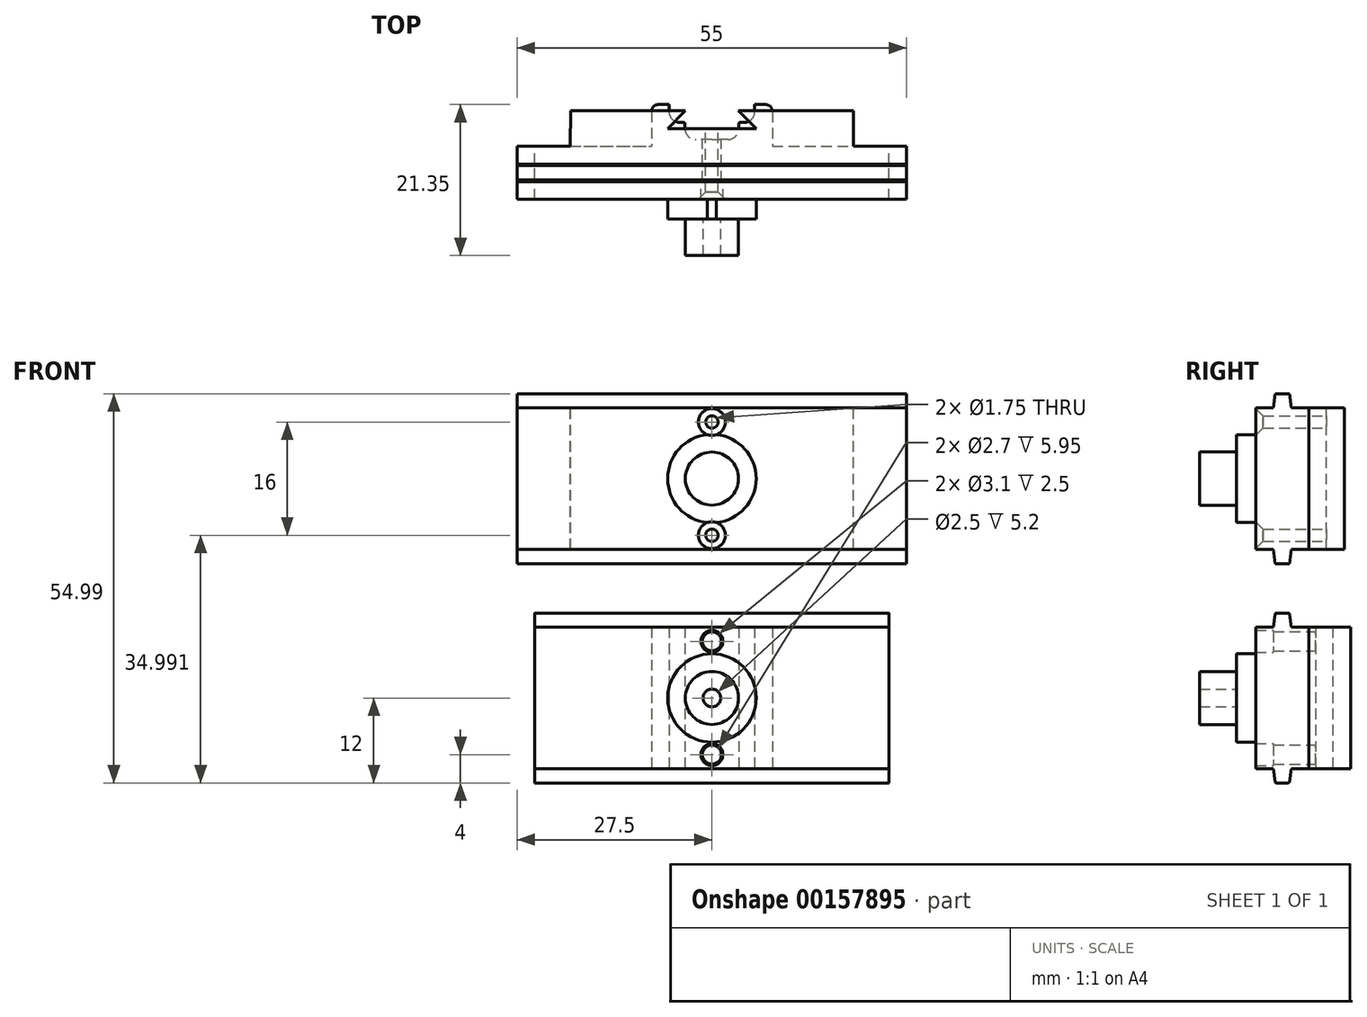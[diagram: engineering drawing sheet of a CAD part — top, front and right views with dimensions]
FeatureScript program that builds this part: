
annotation { "Feature Type Name" : "Feature", "Feature Type Description" : "" }
export const myFeature = defineFeature(function(context is Context, id is Id, definition is map)
    precondition{}
    {
        {
            var Q0;
            Q0=qCreatedBy(makeId("Front.planeOp"),FACE);
            var sketch = newSketch(context, id + "F0", { "sketchPlane" : qUnion([Q0])});
            skLineSegment(sketch, "E0.bottom", {"start": v(-25, 10) * mm, "end": v(25, 10) * mm});
            skLineSegment(sketch, "E0.top", {"start": v(-25, -10) * mm, "end": v(25, -10) * mm});
            skLineSegment(sketch, "E0.left", {"start": v(-25, 10) * mm, "end": v(-25, -10) * mm});
            skLineSegment(sketch, "E0.right", {"start": v(25, 10) * mm, "end": v(25, -10) * mm});
            skSolve(sketch);
        }
        {
            var Q0;
            Q0 = qSketchRegion(id + "F0", true);
            extrude(context, id + "F1", {"entities" : qUnion([Q0]), "depth" : 7.5 * mm, "symmetric" : true});
        }
        {
            var Q0;
            Q0=makeQuery(id+"F1.opExtrude","SWEPT_FACE",FACE,{"disambiguationData":[OSD([sQuery(id+"F0.wireOp",EDGE,"E0.right")])]});
            var sketch = newSketch(context, id + "F2", { "sketchPlane" : qUnion([Q0])});
            skLineSegment(sketch, "E1.bottom", {"start": v(-0.82, 12) * mm, "end": v(0.82, 12) * mm});
            skLineSegment(sketch, "E1.top", {"start": v(-1.25, 10) * mm, "end": v(1.25, 10) * mm});
            skLineSegment(sketch, "E2", {"start": v(1.25, 10) * mm, "end": v(1.02, 11.82) * mm});
            skPoint(sketch, "E3.orphan", {"position": v(1.25, 12) * mm});
            skLineSegment(sketch, "E4.MirrorCS", {"start": v(-1.25, 10) * mm, "end": v(-1.02, 11.82) * mm});
            skPoint(sketch, "E5.visualSharp", {"position": v(-1, 12) * mm});
            skArc(sketch, "E5.filletArc", {"start": v(-0.82, 12) * mm, "mid": v(-0.96, 11.95) * mm, "end": v(-1.02, 11.82) * mm});
            skPoint(sketch, "E6.visualSharp", {"position": v(1, 12) * mm});
            skArc(sketch, "E6.filletArc", {"start": v(1.02, 11.82) * mm, "mid": v(0.96, 11.95) * mm, "end": v(0.82, 12) * mm});
            skLineSegment(sketch, "E7.MirrorCS", {"start": v(1.25, -10) * mm, "end": v(1.02, -11.82) * mm});
            skLineSegment(sketch, "E8.MirrorCS", {"start": v(-1.25, -10) * mm, "end": v(-1.02, -11.82) * mm});
            skLineSegment(sketch, "E9.MirrorCS", {"start": v(-1.25, -10) * mm, "end": v(1.25, -10) * mm});
            skLineSegment(sketch, "E10.MirrorCS", {"start": v(-0.82, -12) * mm, "end": v(0.82, -12) * mm});
            skArc(sketch, "E11.MirrorCS", {"start": v(1.02, -11.82) * mm, "mid": v(0.96, -11.95) * mm, "end": v(0.82, -12) * mm});
            skArc(sketch, "E12.MirrorCS", {"start": v(-0.82, -12) * mm, "mid": v(-0.96, -11.95) * mm, "end": v(-1.02, -11.82) * mm});
            skSolve(sketch);
        }
        {
            var Q0;
            Q0 = qSketchRegion(id + "F2", true);
            extrude(context, id + "F3", {"entities" : qUnion([Q0]), "operationType" : NewBodyOperationType.ADD, "oppositeDirection" : true, "depth" : 50 * mm});
        }
        {
            var Q0;
            Q0=makeQuery(id+"F1.opExtrude","CAP_FACE",FACE,{"disambiguationData":[OSD([sQuery(id+"F0.wireOp",EDGE,"E0.bottom"),sQuery(id+"F0.wireOp",EDGE,"E0.top"),sQuery(id+"F0.wireOp",EDGE,"E0.left"),sQuery(id+"F0.wireOp",EDGE,"E0.right")])],"isStart":false});
            var sketch = newSketch(context, id + "F4", { "sketchPlane" : qUnion([Q0])});
            skCircle(sketch, "E13", {"center": v(0, 0) * mm, "radius": 6.25 * mm});
            skSolve(sketch);
        }
        {
            var Q0;
            Q0 = qSketchRegion(id + "F4", true);
            extrude(context, id + "F5", {"entities" : qUnion([Q0]), "operationType" : NewBodyOperationType.ADD, "depth" : 2.75 * mm});
        }
        {
            var Q0;
            Q0=makeQuery(id+"F5.opExtrude","CAP_FACE",FACE,{"disambiguationData":[OSD([sQuery(id+"F4.wireOp",EDGE,"E13")])],"isStart":false});
            var sketch = newSketch(context, id + "F6", { "sketchPlane" : qUnion([Q0])});
            skCircle(sketch, "E14", {"center": v(0, 0) * mm, "radius": 3.75 * mm});
            skCircle(sketch, "E15", {"center": v(0, 0) * mm, "radius": 1.25 * mm});
            skSolve(sketch);
        }
        {
            var Q0;
            Q0 = qSketchRegion(id + "F6", true);
            extrude(context, id + "F7", {"entities" : qUnion([Q0]), "operationType" : NewBodyOperationType.ADD, "depth" : 5.2 * mm});
        }
        {
            var Q0;
            Q0=qCreatedBy(makeId("Top.planeOp"),FACE);
            var sketch = newSketch(context, id + "F8", { "sketchPlane" : qUnion([Q0])});
            skArc(sketch, "E16.0", {"start": v(-3.8, 6.25) * mm, "mid": v(-3.35, 5.15) * mm, "end": v(-2.25, 4.7) * mm});
            skArc(sketch, "E17.0", {"start": v(-4.5, 7.1) * mm, "mid": v(-5.6, 7.56) * mm, "end": v(-6.05, 8.65) * mm});
            skLineSegment(sketch, "E17.1", {"start": v(-3.96, 7.1) * mm, "end": v(-4.5, 7.1) * mm});
            skLineSegment(sketch, "E18", {"start": v(-3.8, 6.25) * mm, "end": v(-3.8, 6.94) * mm});
            skLineSegment(sketch, "E19", {"start": v(-6.05, 8.65) * mm, "end": v(-6.05, 9.65) * mm});
            skLineSegment(sketch, "E20", {"start": v(-2.25, 4.7) * mm, "end": v(0, 4.7) * mm});
            skPoint(sketch, "E21.orphan", {"position": v(-6, 8.65) * mm});
            skPoint(sketch, "E22.end.orphan", {"position": v(-3.8, 7.15) * mm});
            skLineSegment(sketch, "E23", {"start": v(-6.05, 9.65) * mm, "end": v(-8.55, 9.65) * mm});
            skLineSegment(sketch, "E24.MirrorCS", {"start": v(2.25, 4.7) * mm, "end": v(0, 4.7) * mm});
            skArc(sketch, "E25.MirrorCS", {"start": v(3.8, 6.25) * mm, "mid": v(3.35, 5.15) * mm, "end": v(2.25, 4.7) * mm});
            skLineSegment(sketch, "E26.MirrorCS", {"start": v(3.8, 6.25) * mm, "end": v(3.8, 6.94) * mm});
            skLineSegment(sketch, "E27.MirrorCS", {"start": v(3.96, 7.1) * mm, "end": v(4.5, 7.1) * mm});
            skArc(sketch, "E28.MirrorCS", {"start": v(4.5, 7.1) * mm, "mid": v(5.6, 7.56) * mm, "end": v(6.05, 8.65) * mm});
            skLineSegment(sketch, "E29.MirrorCS", {"start": v(6.05, 8.65) * mm, "end": v(6.05, 9.65) * mm});
            skLineSegment(sketch, "E30.MirrorCS", {"start": v(6.05, 9.65) * mm, "end": v(8.55, 9.65) * mm});
            skPoint(sketch, "E31.orphan", {"position": v(-25, 3.75) * mm});
            skPoint(sketch, "E32.orphan", {"position": v(25, 3.75) * mm});
            skLineSegment(sketch, "E33.0", {"start": v(-8.55, 3.75) * mm, "end": v(8.55, 3.75) * mm});
            skLineSegment(sketch, "E34", {"start": v(8.55, 9.65) * mm, "end": v(8.55, 3.75) * mm});
            skLineSegment(sketch, "E35", {"start": v(-8.55, 9.65) * mm, "end": v(-8.55, 3.75) * mm});
            skPoint(sketch, "E36.visualSharp", {"position": v(3.8, 7.1) * mm});
            skArc(sketch, "E36.filletArc", {"start": v(3.96, 7.1) * mm, "mid": v(3.85, 7.06) * mm, "end": v(3.8, 6.94) * mm});
            skPoint(sketch, "E37.visualSharp", {"position": v(-3.8, 7.1) * mm});
            skArc(sketch, "E37.filletArc", {"start": v(-3.8, 6.94) * mm, "mid": v(-3.85, 7.06) * mm, "end": v(-3.96, 7.1) * mm});
            skSolve(sketch);
        }
        {
            var Q0;
            Q0 = qSketchRegion(id + "F8", true);
            extrude(context, id + "F9", {"entities" : qUnion([Q0]), "operationType" : NewBodyOperationType.ADD, "depth" : 20 * mm, "symmetric" : true});
        }
        {
            var Q0;
            Q0=makeQuery(id+"F9.opExtrude","SWEPT_EDGE",EDGE,{"disambiguationData":[OSD([sQuery(id+"F8.wireOp",EDGE,"E23"),sQuery(id+"F8.wireOp",EDGE,"E35")])]});
            var Q1;
            Q1=makeQuery(id+"F9.opExtrude","SWEPT_EDGE",EDGE,{"disambiguationData":[OSD([sQuery(id+"F8.wireOp",EDGE,"E30.MirrorCS"),sQuery(id+"F8.wireOp",EDGE,"E34")])]});
            var Q2;
            Q2=makeQuery(id+"F9.opExtrude","SWEPT_EDGE",EDGE,{"disambiguationData":[OSD([sQuery(id+"F8.wireOp",EDGE,"E33.0"),sQuery(id+"F8.wireOp",EDGE,"E35")])]});
            var Q3;
            Q3=makeQuery(id+"F9.opExtrude","SWEPT_EDGE",EDGE,{"disambiguationData":[OSD([sQuery(id+"F8.wireOp",EDGE,"E33.0"),sQuery(id+"F8.wireOp",EDGE,"E34")])]});
            fillet(context, id + "F10", {"entities" : qUnion([Q0, Q1, Q2, Q3]), "radius" : 1 * mm, "tangentPropagation" : true, "allowEdgeOverflow" : false});
        }
        {
            var Q0;
            Q0=makeQuery(id+"F1.opExtrude","CAP_FACE",FACE,{"disambiguationData":[OSD([sQuery(id+"F0.wireOp",EDGE,"E0.bottom"),sQuery(id+"F0.wireOp",EDGE,"E0.top"),sQuery(id+"F0.wireOp",EDGE,"E0.left"),sQuery(id+"F0.wireOp",EDGE,"E0.right")])],"isStart":false});
            var sketch = newSketch(context, id + "F11", { "sketchPlane" : qUnion([Q0])});
            skCircle(sketch, "E38", {"center": v(0, 8) * mm, "radius": 1.75 * mm});
            skPoint(sketch, "E38.centerSnap0", {"position": v(0, 10) * mm});
            skCircle(sketch, "E39.MirrorC", {"center": v(0, -8) * mm, "radius": 1.75 * mm});
            skSolve(sketch);
        }
        {
            var Q0;
            Q0=sQuery(id+"F11.wireOp",VERTEX,"E38.center");
            var Q1;
            Q1=sQuery(id+"F11.wireOp",VERTEX,"E39.MirrorC.center");
            var Q2;
            Q2=makeQuery(id+"F1.opExtrude","SWEPT_BODY",BODY,{"disambiguationData":[OSD([sQuery(id+"F0.wireOp",EDGE,"E0.bottom"),sQuery(id+"F0.wireOp",EDGE,"E0.top"),sQuery(id+"F0.wireOp",EDGE,"E0.left"),sQuery(id+"F0.wireOp",EDGE,"E0.right")])]});
            hole(context, id + "F12", {"style" : HoleStyle.C_BORE, "endStyle" : HoleEndStyle.THROUGH, "holeDiameter" : 2.7 * mm, "cBoreDiameter" : 3.1 * mm, "cBoreDepth" : 2.5 * mm, "locations" : qUnion([Q0, Q1]), "scope" : qUnion([Q2]), "isTappedThrough" : true, "startStyle" : HoleStartStyle.SKETCH});
        }
        {
            var Q0;
            Q0=qCreatedBy(makeId("Front.planeOp"),FACE);
            var sketch = newSketch(context, id + "F13", { "sketchPlane" : qUnion([Q0])});
            skLineSegment(sketch, "E40.bottom", {"start": v(27.5, 41) * mm, "end": v(-27.5, 41) * mm});
            skLineSegment(sketch, "E40.top", {"start": v(27.5, 21) * mm, "end": v(-27.5, 21) * mm});
            skLineSegment(sketch, "E40.left", {"start": v(27.5, 41) * mm, "end": v(27.5, 21) * mm});
            skLineSegment(sketch, "E40.right", {"start": v(-27.5, 41) * mm, "end": v(-27.5, 21) * mm});
            skSolve(sketch);
        }
        {
            var Q0;
            Q0=makeQuery(id+"F13.imprint","IMPRINT",FACE,{"disambiguationData":[TD([[makeQuery(id+"F13.imprint","IMPRINT",EDGE,{"derivedFrom":sQuery(id+"F13.wireOp",EDGE,"E40.bottom")}),1.0]])]});
            extrude(context, id + "F14", {"entities" : qUnion([Q0]), "depth" : 7.5 * mm, "symmetric" : true});
        }
        {
            var Q0;
            Q0=makeQuery(id+"F14.opExtrude","SWEPT_FACE",FACE,{"disambiguationData":[OSD([sQuery(id+"F13.wireOp",EDGE,"E40.left")])]});
            var sketch = newSketch(context, id + "F15", { "sketchPlane" : qUnion([Q0])});
            skLineSegment(sketch, "E41.bottom", {"start": v(-1, 43) * mm, "end": v(1, 43) * mm});
            skLineSegment(sketch, "E42", {"start": v(1.25, 41) * mm, "end": v(1, 43) * mm});
            skLineSegment(sketch, "E43.MirrorCS", {"start": v(-1.25, 41) * mm, "end": v(-1, 43) * mm});
            skPoint(sketch, "E44.orphan", {"position": v(1.25, 43) * mm});
            skLineSegment(sketch, "E45", {"start": v(-3.75, 31) * mm, "end": v(3.75, 31) * mm});
            skLineSegment(sketch, "E46.MirrorCS", {"start": v(1.25, 21) * mm, "end": v(1, 19) * mm});
            skLineSegment(sketch, "E47.MirrorCS", {"start": v(-1, 19) * mm, "end": v(1, 19) * mm});
            skLineSegment(sketch, "E48.MirrorCS", {"start": v(-1.25, 21) * mm, "end": v(-1, 19) * mm});
            skPoint(sketch, "E41.top.start.orphan", {"position": v(-1.25, 41) * mm});
            skLineSegment(sketch, "E49.0", {"start": v(-1.25, 41) * mm, "end": v(1.25, 41) * mm});
            skPoint(sketch, "E50.orphan", {"position": v(-3.75, 41) * mm});
            skPoint(sketch, "E51.orphan", {"position": v(3.75, 41) * mm});
            skPoint(sketch, "E52.MirrorCS.end.orphan", {"position": v(1.25, 21) * mm});
            skPoint(sketch, "E52.MirrorCS.start.orphan", {"position": v(-1.25, 21) * mm});
            skLineSegment(sketch, "E53.0", {"start": v(-1.25, 21) * mm, "end": v(1.25, 21) * mm});
            skPoint(sketch, "E54.orphan", {"position": v(3.75, 21) * mm});
            skPoint(sketch, "E55.orphan", {"position": v(-3.75, 21) * mm});
            skLineSegment(sketch, "E56", {"start": v(-1.8, 40.94) * mm, "end": v(1.68, 40.94) * mm});
            skSolve(sketch);
        }
        {
            var Q0;
            Q0 = qSketchRegion(id + "F15", true);
            extrude(context, id + "F16", {"entities" : qUnion([Q0]), "operationType" : NewBodyOperationType.ADD, "oppositeDirection" : true, "depth" : 55 * mm});
        }
        {
            var Q0;
            Q0=makeQuery(id+"F14.opExtrude","CAP_FACE",FACE,{"disambiguationData":[OSD([sQuery(id+"F13.wireOp",EDGE,"E40.bottom"),sQuery(id+"F13.wireOp",EDGE,"E40.top"),sQuery(id+"F13.wireOp",EDGE,"E40.left"),sQuery(id+"F13.wireOp",EDGE,"E40.right")])],"isStart":false});
            var sketch = newSketch(context, id + "F17", { "sketchPlane" : qUnion([Q0])});
            skLineSegment(sketch, "E57", {"start": v(-27.5, 31) * mm, "end": v(27.5, 31) * mm});
            skPoint(sketch, "E58", {"position": v(0, 39) * mm});
            skPoint(sketch, "E59.MirrorP", {"position": v(0, 23) * mm});
            skCircle(sketch, "E60", {"center": v(0, 31) * mm, "radius": 6.25 * mm});
            skSolve(sketch);
        }
        {
            var Q0;
            Q0 = qSketchRegion(id + "F17", true);
            extrude(context, id + "F18", {"entities" : qUnion([Q0]), "operationType" : NewBodyOperationType.ADD, "depth" : 2.75 * mm});
        }
        {
            var Q0;
            Q0=makeQuery(id+"F18.opExtrude","CAP_FACE",FACE,{"disambiguationData":[OSD([sQuery(id+"F17.wireOp",EDGE,"E60")])],"isStart":false});
            var sketch = newSketch(context, id + "F19", { "sketchPlane" : qUnion([Q0])});
            skCircle(sketch, "E61", {"center": v(0, 31) * mm, "radius": 3.75 * mm});
            skSolve(sketch);
        }
        {
            var Q0;
            Q0 = qSketchRegion(id + "F19", true);
            extrude(context, id + "F20", {"entities" : qUnion([Q0]), "operationType" : NewBodyOperationType.ADD, "depth" : 5.2 * mm});
        }
        {
            var Q0;
            {var subQ2=sQuery(id+"F15.wireOp",EDGE,"E42");var subQ6=sQuery(id+"F13.wireOp",EDGE,"E40.bottom");Q0=makeQuery(id+"F16.boolean.opBoolean","SPLIT",FACE,{"disambiguationData":[TD([makeQuery(id+"F16.opExtrude","SWEPT_FACE",FACE,{"disambiguationData":[OSD([subQ2])]})])],"derivedFrom":makeQuery(id+"F14.opExtrude","SWEPT_FACE",FACE,{"disambiguationData":[OSD([subQ6])]})});}
            var sketch = newSketch(context, id + "F21", { "sketchPlane" : qUnion([Q0])});
            skLineSegment(sketch, "E62.top", {"start": v(6.25, 6.25) * mm, "end": v(-6.25, 6.25) * mm});
            skLineSegment(sketch, "E63.top", {"start": v(20, 8.75) * mm, "end": v(3.75, 8.75) * mm});
            skLineSegment(sketch, "E64", {"start": v(-6.25, 6.25) * mm, "end": v(-3.75, 8.75) * mm});
            skLineSegment(sketch, "E65.MirrorCS", {"start": v(6.25, 6.25) * mm, "end": v(3.75, 8.75) * mm});
            skLineSegment(sketch, "E66.trimOffspring", {"start": v(-3.75, 8.75) * mm, "end": v(-19.98, 8.75) * mm});
            skLineSegment(sketch, "E67", {"start": v(-20, 3.75) * mm, "end": v(-19.98, 8.75) * mm});
            skLineSegment(sketch, "E68.0", {"start": v(20, 3.75) * mm, "end": v(-20, 3.75) * mm});
            skLineSegment(sketch, "E69", {"start": v(20, 8.75) * mm, "end": v(20, 3.75) * mm});
            skPoint(sketch, "E70.orphan", {"position": v(27.5, 3.75) * mm});
            skPoint(sketch, "E71.orphan", {"position": v(-27.5, 3.75) * mm});
            skSolve(sketch);
        }
        {
            var Q0;
            Q0 = qSketchRegion(id + "F21", true);
            extrude(context, id + "F22", {"entities" : qUnion([Q0]), "operationType" : NewBodyOperationType.ADD, "oppositeDirection" : true, "depth" : 20 * mm});
        }
        {
            var Q0;
            Q0=sQuery(id+"F17.wireOp",VERTEX,"E58");
            var Q1;
            Q1=sQuery(id+"F17.wireOp",VERTEX,"E59.MirrorP");
            var Q2;
            Q2=makeQuery(id+"F14.opExtrude","SWEPT_BODY",BODY,{"disambiguationData":[OSD([sQuery(id+"F13.wireOp",EDGE,"E40.bottom"),sQuery(id+"F13.wireOp",EDGE,"E40.top"),sQuery(id+"F13.wireOp",EDGE,"E40.left"),sQuery(id+"F13.wireOp",EDGE,"E40.right")])]});
            hole(context, id + "F23", {"style" : HoleStyle.C_SINK, "endStyle" : HoleEndStyle.THROUGH, "holeDiameter" : 1.75 * mm, "cSinkDiameter" : 3.8 * mm, "cSinkAngle" : 90 * degree, "locations" : qUnion([Q0, Q1]), "scope" : qUnion([Q2]), "isTappedThrough" : true, "startStyle" : HoleStartStyle.SKETCH});
        }
    });
